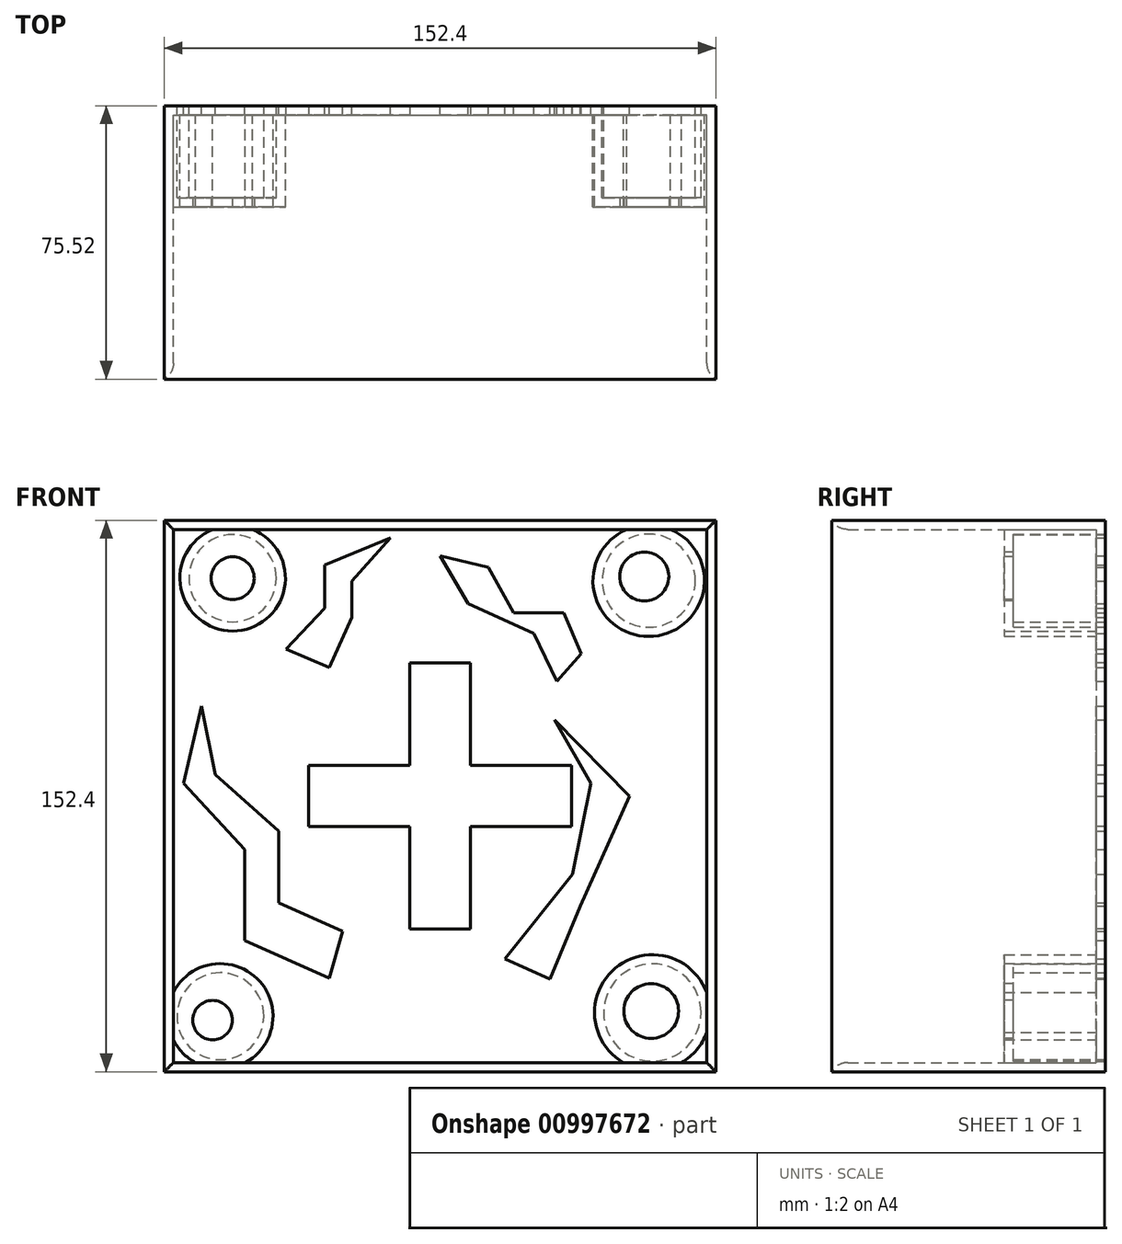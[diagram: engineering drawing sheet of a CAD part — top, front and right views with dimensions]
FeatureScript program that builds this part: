
annotation { "Feature Type Name" : "Feature", "Feature Type Description" : "" }
export const myFeature = defineFeature(function(context is Context, id is Id, definition is map)
    precondition{}
    {
        {
            var Q0;
            Q0=qCreatedBy(makeId("Front.planeOp"),FACE);
            var sketch = newSketch(context, id + "F0", { "sketchPlane" : qUnion([Q0])});
            skLineSegment(sketch, "E0.bottom", {"start": v(-76.2, 76.2) * mm, "end": v(76.2, 76.2) * mm});
            skLineSegment(sketch, "E0.top", {"start": v(-76.2, -76.2) * mm, "end": v(76.2, -76.2) * mm});
            skLineSegment(sketch, "E0.left", {"start": v(-76.2, 76.2) * mm, "end": v(-76.2, -76.2) * mm});
            skLineSegment(sketch, "E0.right", {"start": v(76.2, 76.2) * mm, "end": v(76.2, -76.2) * mm});
            skSolve(sketch);
        }
        {
            var Q0;
            Q0=makeQuery(id+"F0.imprint","IMPRINT",FACE,{"disambiguationData":[TD([[makeQuery(id+"F0.imprint","IMPRINT",EDGE,{"derivedFrom":sQuery(id+"F0.wireOp",EDGE,"E0.bottom")}),-1.0]])]});
            extrude(context, id + "F1", {"entities" : qUnion([Q0]), "depth" : 76.2 * mm, "offsetDistance" : 25.4 * mm});
        }
        {
            var Q0;
            Q0=makeQuery(id+"F0.imprint","IMPRINT",FACE,{"disambiguationData":[TD([[makeQuery(id+"F0.imprint","IMPRINT",EDGE,{"derivedFrom":sQuery(id+"F0.wireOp",EDGE,"E0.bottom")}),-1.0]])]});
            var sketch = newSketch(context, id + "F2", { "sketchPlane" : qUnion([Q0])});
            skCircle(sketch, "E1", {"center": v(57.63, 59.5) * mm, "radius": 12.87 * mm});
            skCircle(sketch, "E2", {"center": v(-57.3, 60.18) * mm, "radius": 12.04 * mm});
            skCircle(sketch, "E3", {"center": v(58.65, -59.84) * mm, "radius": 13.45 * mm});
            skCircle(sketch, "E4", {"center": v(-60.69, -60.86) * mm, "radius": 12 * mm});
            skSolve(sketch);
        }
        {
            var Q0;
            Q0 = qSketchRegion(id + "F2", true);
            var Q1;
            Q1=makeQuery(id+"F2.imprint","IMPRINT",FACE,{"disambiguationData":[TD([[makeQuery(id+"F2.imprint","IMPRINT",EDGE,{"derivedFrom":sQuery(id+"F2.wireOp",EDGE,"E1")}),1.0]])]});
            extrude(context, id + "F3", {"entities" : qUnion([Q0, Q1]), "operationType" : NewBodyOperationType.REMOVE, "depth" : 25.4 * mm, "offsetDistance" : 25.4 * mm});
        }
        {
            var Q0;
            Q0=makeQuery(id+"F1.opExtrude","CAP_FACE",FACE,{"disambiguationData":[OSD([sQuery(id+"F0.wireOp",EDGE,"E0.bottom"),sQuery(id+"F0.wireOp",EDGE,"E0.top"),sQuery(id+"F0.wireOp",EDGE,"E0.left"),sQuery(id+"F0.wireOp",EDGE,"E0.right")])],"isStart":false});
            shell(context, id + "F4", {"entities" : qUnion([Q0]), "thickness" : 2.54 * mm});
        }
        {
            var Q0;
            {var subQ0=sQuery(id+"F0.wireOp",EDGE,"E0.bottom");Q0=makeQuery(id+"F4.opShell","OFFSET_EDGE",EDGE,{"disambiguationData":[OSD([subQ0]),TDD([makeQuery(id+"F1.opExtrude","CAP_EDGE",EDGE,{"disambiguationData":[OSD([subQ0])],"isStart":false})])]});}
            var Q1;
            {var subQ0=sQuery(id+"F0.wireOp",EDGE,"E0.left");Q1=makeQuery(id+"F4.opShell","OFFSET_EDGE",EDGE,{"disambiguationData":[OSD([subQ0]),TDD([makeQuery(id+"F1.opExtrude","CAP_EDGE",EDGE,{"disambiguationData":[OSD([subQ0])],"isStart":false})])]});}
            var Q2;
            {var subQ0=sQuery(id+"F0.wireOp",EDGE,"E0.top");Q2=makeQuery(id+"F4.opShell","OFFSET_EDGE",EDGE,{"disambiguationData":[OSD([subQ0]),TDD([makeQuery(id+"F1.opExtrude","CAP_EDGE",EDGE,{"disambiguationData":[OSD([subQ0])],"isStart":false})])]});}
            var Q3;
            {var subQ0=sQuery(id+"F0.wireOp",EDGE,"E0.right");Q3=makeQuery(id+"F4.opShell","OFFSET_EDGE",EDGE,{"disambiguationData":[OSD([subQ0]),TDD([makeQuery(id+"F1.opExtrude","CAP_EDGE",EDGE,{"disambiguationData":[OSD([subQ0])],"isStart":false})])]});}
            fillet(context, id + "F5", {"entities" : qUnion([Q0, Q1, Q2, Q3]), "radius" : 5.08 * mm, "tangentPropagation" : true, "allowEdgeOverflow" : false});
        }
        {
            var Q0;
            Q0=makeQuery(id+"F4.opShell","OFFSET_FACE",FACE,{"disambiguationData":[OSD([sQuery(id+"F0.wireOp",EDGE,"E0.bottom"),sQuery(id+"F0.wireOp",EDGE,"E0.top"),sQuery(id+"F0.wireOp",EDGE,"E0.left"),sQuery(id+"F0.wireOp",EDGE,"E0.right")]),OD(2.0)]});
            var sketch = newSketch(context, id + "F6", { "sketchPlane" : qUnion([Q0])});
            skLineSegment(sketch, "E5.bottom", {"start": v(-8.33, 36.78) * mm, "end": v(8.33, 36.78) * mm});
            skLineSegment(sketch, "E5.top", {"start": v(-8.33, -36.78) * mm, "end": v(8.33, -36.78) * mm});
            skLineSegment(sketch, "E5.left", {"start": v(-8.33, 36.78) * mm, "end": v(-8.33, -36.78) * mm});
            skLineSegment(sketch, "E5.right", {"start": v(8.33, 36.78) * mm, "end": v(8.33, -36.78) * mm});
            skPoint(sketch, "E5.middle", {"position": v(0, 0) * mm});
            skLineSegment(sketch, "E6.bottom", {"start": v(36.31, -8.49) * mm, "end": v(-36.31, -8.49) * mm});
            skLineSegment(sketch, "E6.top", {"start": v(36.31, 8.49) * mm, "end": v(-36.31, 8.49) * mm});
            skLineSegment(sketch, "E6.left", {"start": v(36.31, -8.49) * mm, "end": v(36.31, 8.49) * mm});
            skLineSegment(sketch, "E6.right", {"start": v(-36.31, -8.49) * mm, "end": v(-36.31, 8.49) * mm});
            skSolve(sketch);
        }
        {
            var Q0;
            {var subQ0=sQuery(id+"F6.wireOp",EDGE,"E5.bottom");Q0=makeQuery(id+"F6.imprint","IMPRINT",FACE,{"disambiguationData":[TD([[makeQuery(id+"F6.imprint","IMPRINT",EDGE,{"derivedFrom":subQ0}),-1.0]])]});}
            var Q1;
            {var subQ0=sQuery(id+"F6.wireOp",EDGE,"E6.top");var subQ1=sQuery(id+"F6.wireOp",EDGE,"E5.left");var subQ2=makeQuery(id+"F6.imprint","INTERSECT",VERTEX,{"derivedFrom":[subQ1,subQ0]});Q1=makeQuery(id+"F6.imprint","IMPRINT",FACE,{"disambiguationData":[TD([[makeQuery(id+"F6.imprint","IMPRINT",EDGE,{"disambiguationData":[TD([[subQ2,-1.0]])],"derivedFrom":subQ1}),1.0]])]});}
            var Q2;
            {var subQ0=sQuery(id+"F6.wireOp",EDGE,"E5.top");Q2=makeQuery(id+"F6.imprint","IMPRINT",FACE,{"disambiguationData":[TD([[makeQuery(id+"F6.imprint","IMPRINT",EDGE,{"derivedFrom":subQ0}),1.0]])]});}
            var Q3;
            {var subQ5=sQuery(id+"F6.wireOp",EDGE,"E6.left");Q3=makeQuery(id+"F6.imprint","IMPRINT",FACE,{"disambiguationData":[TD([[makeQuery(id+"F6.imprint","IMPRINT",EDGE,{"derivedFrom":subQ5}),1.0]])]});}
            var Q4;
            {var subQ5=sQuery(id+"F6.wireOp",EDGE,"E6.right");Q4=makeQuery(id+"F6.imprint","IMPRINT",FACE,{"disambiguationData":[TD([[makeQuery(id+"F6.imprint","IMPRINT",EDGE,{"derivedFrom":subQ5}),-1.0]])]});}
            extrude(context, id + "F7", {"entities" : qUnion([Q0, Q1, Q2, Q3, Q4]), "operationType" : NewBodyOperationType.REMOVE, "oppositeDirection" : true, "depth" : 25.4 * mm, "offsetDistance" : 25.4 * mm});
        }
        {
            var Q0;
            {var subQ0=sQuery(id+"F2.wireOp",EDGE,"E2");Q0=makeQuery(id+"F4.opShell","OFFSET_FACE",FACE,{"disambiguationData":[OSD([subQ0]),TDD([makeQuery(id+"F3.boolean.opBoolean","COPY",FACE,{"derivedFrom":makeQuery(id+"F3.opExtrude","CAP_FACE",FACE,{"disambiguationData":[OSD([subQ0])],"isStart":false})})])]});}
            var sketch = newSketch(context, id + "F8", { "sketchPlane" : qUnion([Q0])});
            skCircle(sketch, "E7", {"center": v(-57.3, 60.18) * mm, "radius": 5.93 * mm});
            skCircle(sketch, "E8", {"center": v(56.43, 60.68) * mm, "radius": 6.77 * mm});
            skCircle(sketch, "E9", {"center": v(58.32, -59.42) * mm, "radius": 7.57 * mm});
            skCircle(sketch, "E10", {"center": v(-62.84, -61.93) * mm, "radius": 5.45 * mm});
            skSolve(sketch);
        }
        {
            var Q0;
            Q0=makeQuery(id+"F8.imprint","IMPRINT",FACE,{"disambiguationData":[TD([[makeQuery(id+"F8.imprint","IMPRINT",EDGE,{"derivedFrom":sQuery(id+"F8.wireOp",EDGE,"E10")}),1.0]])]});
            var Q1;
            Q1=makeQuery(id+"F8.imprint","IMPRINT",FACE,{"disambiguationData":[TD([[makeQuery(id+"F8.imprint","IMPRINT",EDGE,{"derivedFrom":sQuery(id+"F8.wireOp",EDGE,"E7")}),1.0]])]});
            var Q2;
            Q2=makeQuery(id+"F8.imprint","IMPRINT",FACE,{"disambiguationData":[TD([[makeQuery(id+"F8.imprint","IMPRINT",EDGE,{"derivedFrom":sQuery(id+"F8.wireOp",EDGE,"E8")}),1.0]])]});
            var Q3;
            Q3=makeQuery(id+"F8.imprint","IMPRINT",FACE,{"disambiguationData":[TD([[makeQuery(id+"F8.imprint","IMPRINT",EDGE,{"derivedFrom":sQuery(id+"F8.wireOp",EDGE,"E9")}),1.0]])]});
            extrude(context, id + "F9", {"entities" : qUnion([Q0, Q1, Q2, Q3]), "operationType" : NewBodyOperationType.REMOVE, "oppositeDirection" : true, "depth" : 25.4 * mm, "offsetDistance" : 25.4 * mm});
        }
        {
            var Q0;
            Q0=makeQuery(id+"F0.imprint","IMPRINT",FACE,{"disambiguationData":[TD([[makeQuery(id+"F0.imprint","IMPRINT",EDGE,{"derivedFrom":sQuery(id+"F0.wireOp",EDGE,"E0.bottom")}),-1.0]])]});
            var sketch = newSketch(context, id + "F10", { "sketchPlane" : qUnion([Q0])});
            skLineSegment(sketch, "E11", {"start": v(39.77, 37.41) * mm, "end": v(34.11, 50.62) * mm});
            skLineSegment(sketch, "E12", {"start": v(34.11, 50.62) * mm, "end": v(20.28, 50.62) * mm});
            skLineSegment(sketch, "E13", {"start": v(20.28, 50.62) * mm, "end": v(13.36, 63.2) * mm});
            skLineSegment(sketch, "E14", {"start": v(13.36, 63.2) * mm, "end": v(0, 66.33) * mm});
            skLineSegment(sketch, "E15", {"start": v(0, 66.33) * mm, "end": v(7.7, 53.13) * mm});
            skLineSegment(sketch, "E16", {"start": v(7.7, 53.13) * mm, "end": v(25.94, 44.96) * mm});
            skLineSegment(sketch, "E17", {"start": v(25.94, 44.96) * mm, "end": v(32.22, 31.75) * mm});
            skLineSegment(sketch, "E18", {"start": v(32.22, 31.75) * mm, "end": v(38.96, 39.3) * mm});
            skLineSegment(sketch, "E19", {"start": v(-30.65, 35.53) * mm, "end": v(-42.6, 40.56) * mm});
            skLineSegment(sketch, "E20", {"start": v(-42.6, 40.56) * mm, "end": v(-31.9, 51.87) * mm});
            skLineSegment(sketch, "E21", {"start": v(-31.9, 51.87) * mm, "end": v(-31.9, 63.82) * mm});
            skLineSegment(sketch, "E22", {"start": v(-31.9, 63.82) * mm, "end": v(-13.68, 71.36) * mm});
            skLineSegment(sketch, "E23", {"start": v(-13.68, 71.36) * mm, "end": v(-24.36, 59.42) * mm});
            skLineSegment(sketch, "E24", {"start": v(-24.36, 59.42) * mm, "end": v(-24.36, 49.36) * mm});
            skLineSegment(sketch, "E25", {"start": v(-24.36, 49.36) * mm, "end": v(-30.65, 35.53) * mm});
            skLineSegment(sketch, "E26", {"start": v(-26.88, -37.41) * mm, "end": v(-44.54, -29.5) * mm});
            skLineSegment(sketch, "E27", {"start": v(-44.54, -29.5) * mm, "end": v(-44.54, -9.75) * mm});
            skLineSegment(sketch, "E28", {"start": v(-44.54, -9.75) * mm, "end": v(-62.1, 5.97) * mm});
            skLineSegment(sketch, "E29", {"start": v(-62.1, 5.97) * mm, "end": v(-65.86, 24.84) * mm});
            skLineSegment(sketch, "E30", {"start": v(-65.86, 24.84) * mm, "end": v(-70.9, 3.46) * mm});
            skLineSegment(sketch, "E31", {"start": v(-70.9, 3.46) * mm, "end": v(-53.92, -14.78) * mm});
            skLineSegment(sketch, "E32", {"start": v(-53.92, -14.78) * mm, "end": v(-53.92, -39.93) * mm});
            skLineSegment(sketch, "E33", {"start": v(-53.92, -39.93) * mm, "end": v(-30.65, -50.36) * mm});
            skLineSegment(sketch, "E34", {"start": v(-30.65, -50.36) * mm, "end": v(-26.88, -37.41) * mm});
            skLineSegment(sketch, "E35", {"start": v(30.34, -50.62) * mm, "end": v(17.93, -45.06) * mm});
            skLineSegment(sketch, "E36", {"start": v(17.93, -45.06) * mm, "end": v(36.63, -21.7) * mm});
            skLineSegment(sketch, "E37", {"start": v(36.63, -21.7) * mm, "end": v(41.66, 3.46) * mm});
            skLineSegment(sketch, "E38", {"start": v(41.66, 3.46) * mm, "end": v(31.6, 21.06) * mm});
            skLineSegment(sketch, "E39", {"start": v(31.6, 21.06) * mm, "end": v(52.34, 0) * mm});
            skLineSegment(sketch, "E40", {"start": v(52.34, 0) * mm, "end": v(38.73, -30.38) * mm});
            skLineSegment(sketch, "E41", {"start": v(38.73, -30.38) * mm, "end": v(30.34, -50.62) * mm});
            skSolve(sketch);
        }
        {
            var Q0;
            Q0=makeQuery(id+"F10.imprint","IMPRINT",FACE,{"disambiguationData":[TD([[makeQuery(id+"F10.imprint","IMPRINT",EDGE,{"derivedFrom":sQuery(id+"F10.wireOp",EDGE,"E35")}),-1.0]])]});
            var Q1;
            Q1=makeQuery(id+"F10.imprint","IMPRINT",FACE,{"disambiguationData":[TD([[makeQuery(id+"F10.imprint","IMPRINT",EDGE,{"derivedFrom":sQuery(id+"F10.wireOp",EDGE,"E26")}),1.0]])]});
            var Q2;
            Q2=makeQuery(id+"F10.imprint","IMPRINT",FACE,{"disambiguationData":[TD([[makeQuery(id+"F10.imprint","IMPRINT",EDGE,{"derivedFrom":sQuery(id+"F10.wireOp",EDGE,"E19")}),-1.0]])]});
            var Q3;
            {var subQ0=sQuery(id+"F10.wireOp",EDGE,"E12");Q3=makeQuery(id+"F10.imprint","IMPRINT",FACE,{"disambiguationData":[TD([[makeQuery(id+"F10.imprint","IMPRINT",EDGE,{"derivedFrom":subQ0}),1.0]])]});}
            extrude(context, id + "F11", {"entities" : qUnion([Q0, Q1, Q2, Q3]), "operationType" : NewBodyOperationType.REMOVE, "depth" : 25.4 * mm, "offsetDistance" : 25.4 * mm});
        }
    });
